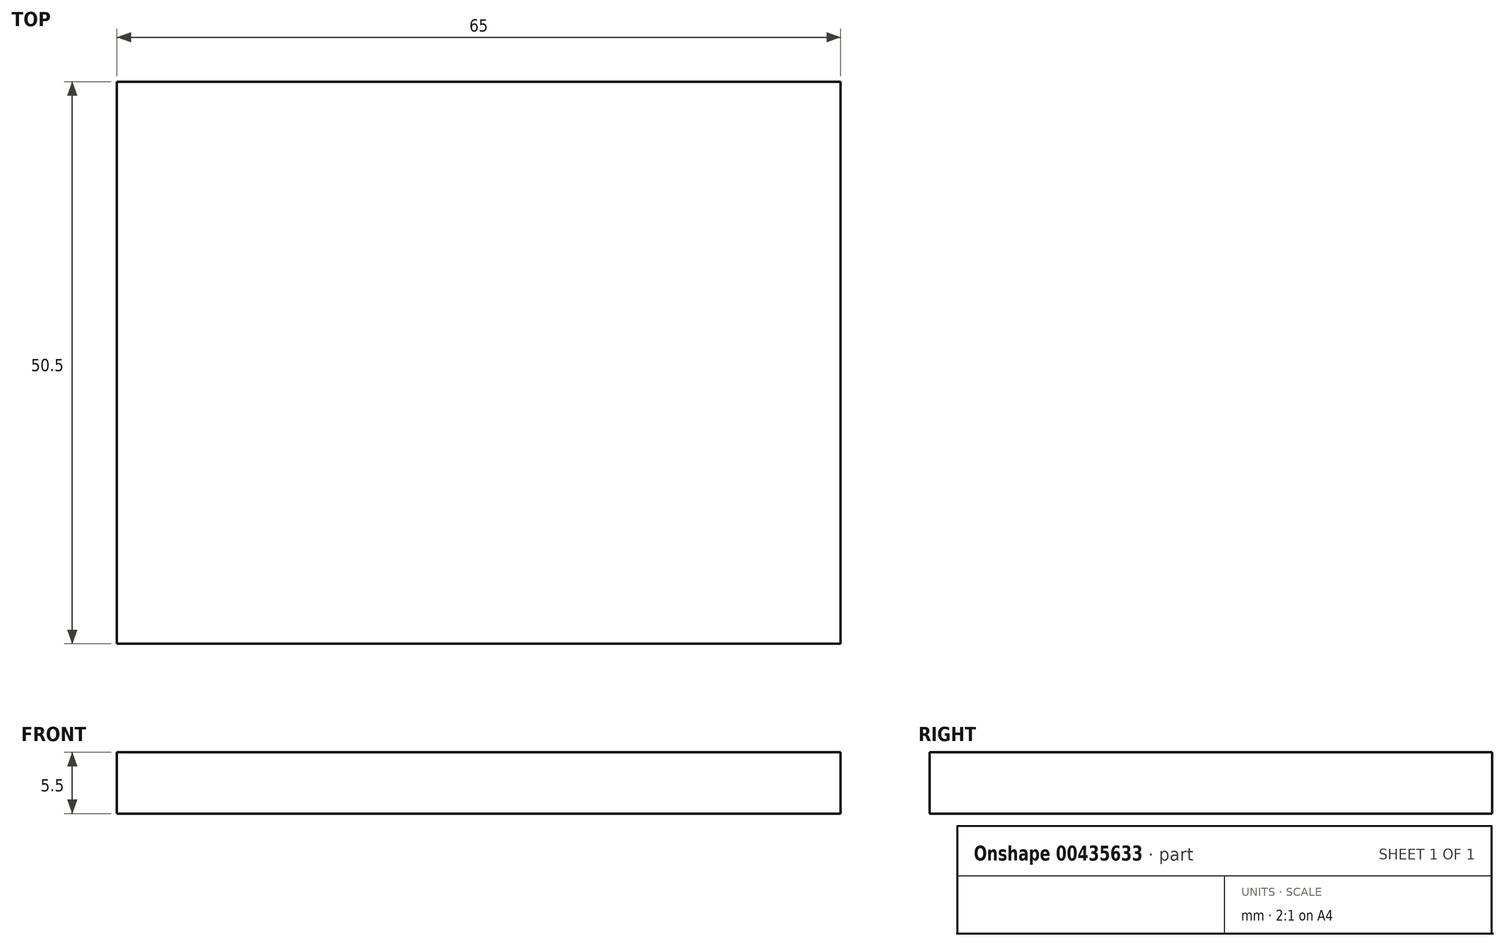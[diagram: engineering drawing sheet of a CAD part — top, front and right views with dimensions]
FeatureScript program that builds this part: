
annotation { "Feature Type Name" : "Feature", "Feature Type Description" : "" }
export const myFeature = defineFeature(function(context is Context, id is Id, definition is map)
    precondition{}
    {
        {
            var Q0;
            Q0=qCreatedBy(makeId("Top.planeOp"),FACE);
            var sketch = newSketch(context, id + "F0", { "sketchPlane" : qUnion([Q0])});
            skLineSegment(sketch, "E0.bottom", {"start": v(-32.5, 25.25) * mm, "end": v(32.5, 25.25) * mm});
            skLineSegment(sketch, "E0.top", {"start": v(-32.5, -25.25) * mm, "end": v(32.5, -25.25) * mm});
            skLineSegment(sketch, "E0.left", {"start": v(-32.5, 25.25) * mm, "end": v(-32.5, -25.25) * mm});
            skLineSegment(sketch, "E0.right", {"start": v(32.5, 25.25) * mm, "end": v(32.5, -25.25) * mm});
            skPoint(sketch, "E0.middle", {"position": v(0, 0) * mm});
            skSolve(sketch);
        }
        {
            var Q0;
            Q0=makeQuery(id+"F0.imprint","IMPRINT",FACE,{"disambiguationData":[TD([[makeQuery(id+"F0.imprint","IMPRINT",EDGE,{"derivedFrom":sQuery(id+"F0.wireOp",EDGE,"E0.bottom")}),-1.0]])]});
            extrude(context, id + "F1", {"entities" : qUnion([Q0]), "depth" : 5.5 * mm});
        }
    });
